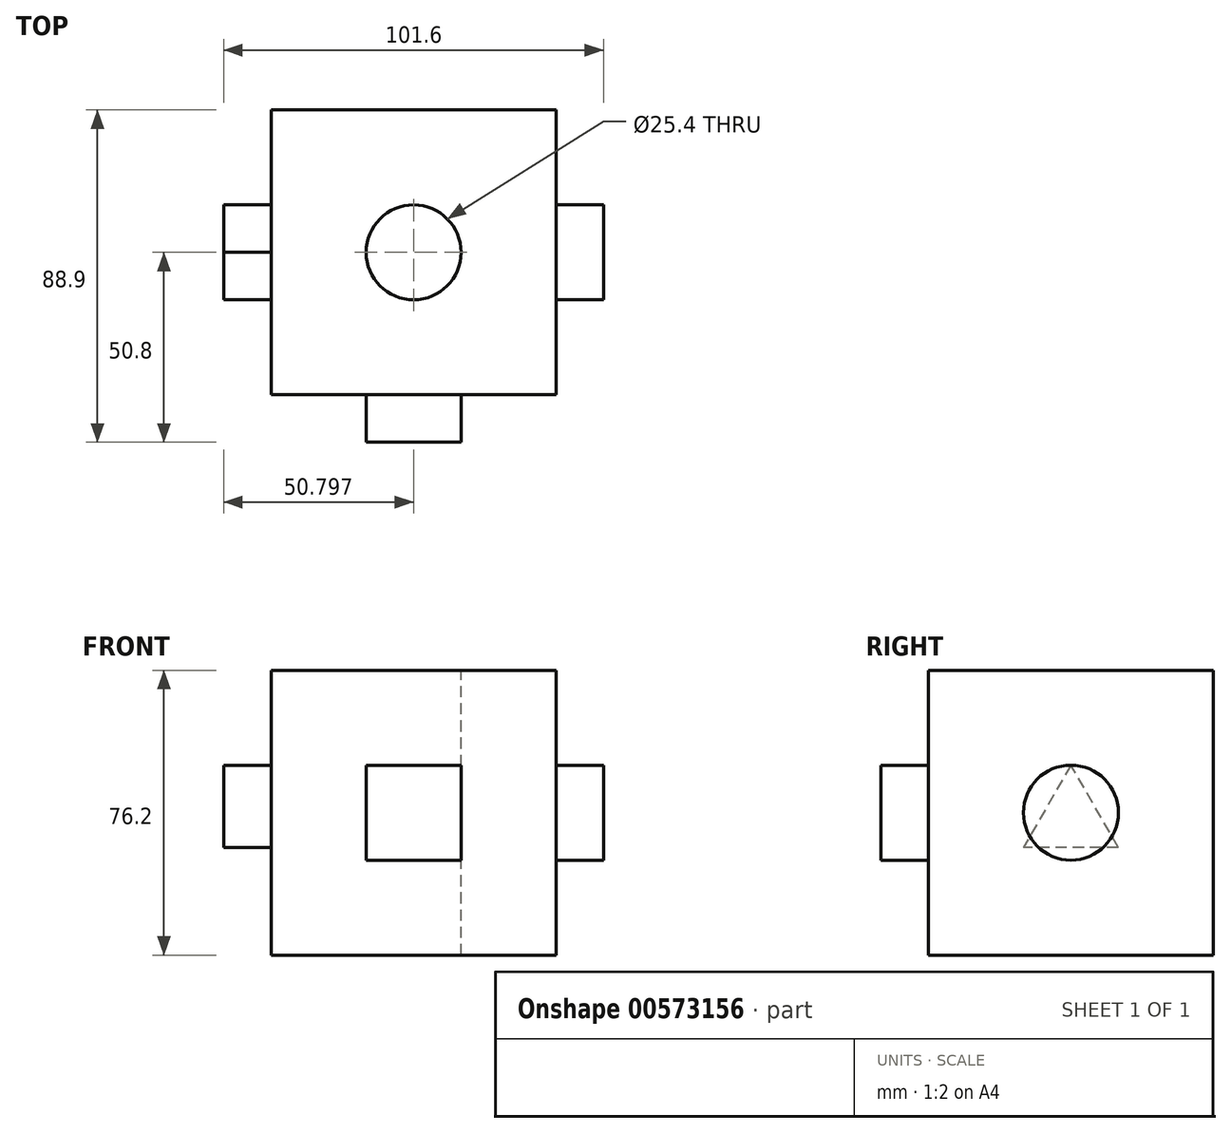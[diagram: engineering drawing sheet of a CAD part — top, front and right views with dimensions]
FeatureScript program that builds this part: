
annotation { "Feature Type Name" : "Feature", "Feature Type Description" : "" }
export const myFeature = defineFeature(function(context is Context, id is Id, definition is map)
    precondition{}
    {
        {
            var Q0;
            Q0=qCreatedBy(makeId("Front.planeOp"),FACE);
            var sketch = newSketch(context, id + "F0", { "sketchPlane" : qUnion([Q0])});
            skLineSegment(sketch, "E0.bottom", {"start": v(-33.18, 58.5) * mm, "end": v(43.02, 58.5) * mm});
            skLineSegment(sketch, "E0.top", {"start": v(-33.18, -17.7) * mm, "end": v(43.02, -17.7) * mm});
            skLineSegment(sketch, "E0.left", {"start": v(-33.18, 58.5) * mm, "end": v(-33.18, -17.7) * mm});
            skLineSegment(sketch, "E0.right", {"start": v(43.02, 58.5) * mm, "end": v(43.02, -17.7) * mm});
            skSolve(sketch);
        }
        {
            var Q0;
            Q0=makeQuery(id+"F0.imprint","IMPRINT",FACE,{"disambiguationData":[TD([[makeQuery(id+"F0.imprint","IMPRINT",EDGE,{"derivedFrom":sQuery(id+"F0.wireOp",EDGE,"E0.bottom")}),-1.0]])]});
            extrude(context, id + "F1", {"entities" : qUnion([Q0]), "depth" : 76.2 * mm, "offsetDistance" : 25.4 * mm});
        }
        {
            var Q0;
            Q0=makeQuery(id+"F1.opExtrude","CAP_FACE",FACE,{"disambiguationData":[OSD([sQuery(id+"F0.wireOp",EDGE,"E0.bottom"),sQuery(id+"F0.wireOp",EDGE,"E0.top"),sQuery(id+"F0.wireOp",EDGE,"E0.left"),sQuery(id+"F0.wireOp",EDGE,"E0.right")])],"isStart":false});
            var sketch = newSketch(context, id + "F2", { "sketchPlane" : qUnion([Q0])});
            skLineSegment(sketch, "E1.bottom", {"start": v(-7.78, 33.1) * mm, "end": v(17.62, 33.1) * mm});
            skLineSegment(sketch, "E1.top", {"start": v(-7.78, 7.7) * mm, "end": v(17.62, 7.7) * mm});
            skLineSegment(sketch, "E1.left", {"start": v(-7.78, 33.1) * mm, "end": v(-7.78, 7.7) * mm});
            skLineSegment(sketch, "E1.right", {"start": v(17.62, 33.1) * mm, "end": v(17.62, 7.7) * mm});
            skSolve(sketch);
        }
        {
            var Q0;
            Q0=makeQuery(id+"F2.imprint","IMPRINT",FACE,{"disambiguationData":[TD([[makeQuery(id+"F2.imprint","IMPRINT",EDGE,{"derivedFrom":sQuery(id+"F2.wireOp",EDGE,"E1.bottom")}),-1.0]])]});
            extrude(context, id + "F3", {"entities" : qUnion([Q0]), "operationType" : NewBodyOperationType.ADD, "depth" : 12.7 * mm, "offsetDistance" : 25.4 * mm});
        }
        {
            var Q0;
            Q0=makeQuery(id+"F1.opExtrude","SWEPT_FACE",FACE,{"disambiguationData":[OSD([sQuery(id+"F0.wireOp",EDGE,"E0.right")])]});
            var sketch = newSketch(context, id + "F4", { "sketchPlane" : qUnion([Q0])});
            skCircle(sketch, "E2", {"center": v(-38.1, 20.4) * mm, "radius": 12.7 * mm});
            skSolve(sketch);
        }
        {
            var Q0;
            Q0=makeQuery(id+"F4.imprint","IMPRINT",FACE,{"disambiguationData":[TD([[makeQuery(id+"F4.imprint","IMPRINT",EDGE,{"derivedFrom":sQuery(id+"F4.wireOp",EDGE,"E2")}),1.0]])]});
            extrude(context, id + "F5", {"entities" : qUnion([Q0]), "operationType" : NewBodyOperationType.ADD, "depth" : 12.7 * mm, "offsetDistance" : 25.4 * mm});
        }
        {
            var Q0;
            Q0=makeQuery(id+"F1.opExtrude","SWEPT_FACE",FACE,{"disambiguationData":[OSD([sQuery(id+"F0.wireOp",EDGE,"E0.bottom")])]});
            var sketch = newSketch(context, id + "F6", { "sketchPlane" : qUnion([Q0])});
            skPoint(sketch, "E3", {"position": v(4.92, -38.1) * mm});
            skPoint(sketch, "E3.positionSnap0", {"position": v(4.92, 0) * mm});
            skSolve(sketch);
        }
        {
            var Q0;
            Q0=sQuery(id+"F6.wireOp",VERTEX,"E3");
            var Q1;
            Q1=makeQuery(id+"F1.opExtrude","SWEPT_BODY",BODY,{"disambiguationData":[OSD([sQuery(id+"F0.wireOp",EDGE,"E0.bottom"),sQuery(id+"F0.wireOp",EDGE,"E0.top"),sQuery(id+"F0.wireOp",EDGE,"E0.left"),sQuery(id+"F0.wireOp",EDGE,"E0.right")])]});
            hole(context, id + "F7", {"style" : HoleStyle.SIMPLE, "endStyle" : HoleEndStyle.THROUGH, "holeDiameter" : 25.4 * mm, "isTappedThrough" : true, "tappedDepth" : 12.7 * mm, "tapClearance" : 3, "locations" : qUnion([Q0]), "scope" : qUnion([Q1])});
        }
        {
            var Q0;
            Q0=makeQuery(id+"F1.opExtrude","SWEPT_FACE",FACE,{"disambiguationData":[OSD([sQuery(id+"F0.wireOp",EDGE,"E0.left")])]});
            var sketch = newSketch(context, id + "F8", { "sketchPlane" : qUnion([Q0])});
            skLineSegment(sketch, "E4", {"start": v(25.4, 11.1) * mm, "end": v(38.1, 33.1) * mm});
            skLineSegment(sketch, "E5", {"start": v(38.1, 33.1) * mm, "end": v(50.8, 11.1) * mm});
            skLineSegment(sketch, "E6", {"start": v(25.4, 11.1) * mm, "end": v(50.8, 11.1) * mm});
            skSolve(sketch);
        }
        {
            var Q0;
            Q0=makeQuery(id+"F8.imprint","IMPRINT",FACE,{"disambiguationData":[TD([[makeQuery(id+"F8.imprint","IMPRINT",EDGE,{"derivedFrom":sQuery(id+"F8.wireOp",EDGE,"E4")}),-1.0]])]});
            extrude(context, id + "F9", {"entities" : qUnion([Q0]), "operationType" : NewBodyOperationType.ADD, "depth" : 12.7 * mm, "offsetDistance" : 25.4 * mm});
        }
    });
